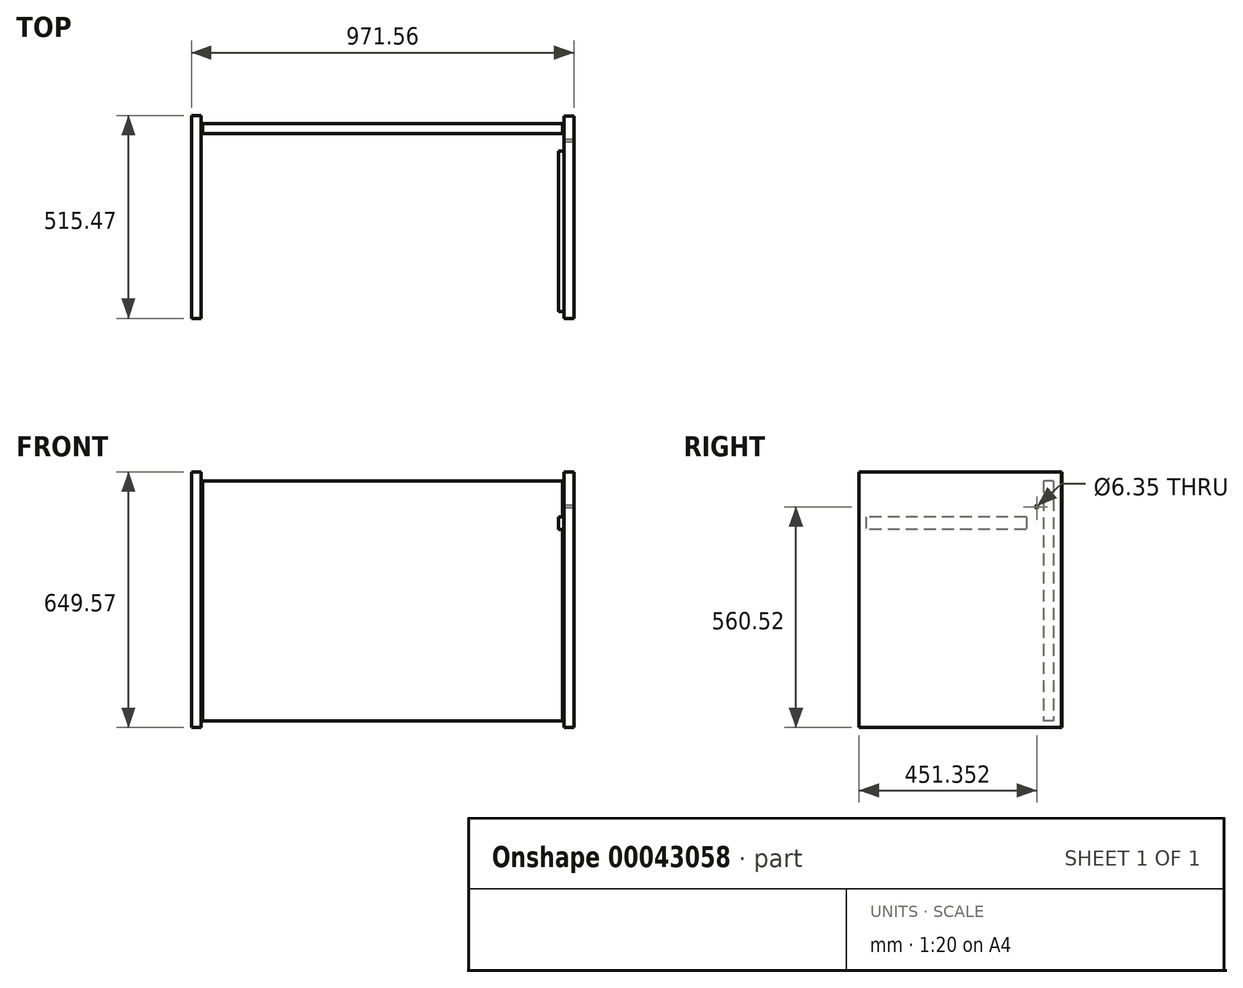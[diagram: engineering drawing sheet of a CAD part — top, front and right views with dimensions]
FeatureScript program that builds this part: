
annotation { "Feature Type Name" : "Feature", "Feature Type Description" : "" }
export const myFeature = defineFeature(function(context is Context, id is Id, definition is map)
    precondition{}
    {
        {
            var Q0;
            Q0=qCreatedBy(makeId("Front.planeOp"),FACE);
            var sketch = newSketch(context, id + "F0", { "sketchPlane" : qUnion([Q0])});
            skLineSegment(sketch, "E0.rect.bottom", {"start": v(457.2, 304.8) * mm, "end": v(-457.2, 304.8) * mm});
            skLineSegment(sketch, "E0.rect.top", {"start": v(457.2, -304.8) * mm, "end": v(-457.2, -304.8) * mm});
            skLineSegment(sketch, "E0.rect.left", {"start": v(457.2, 304.8) * mm, "end": v(457.2, -304.8) * mm});
            skLineSegment(sketch, "E0.rect.right", {"start": v(-457.2, 304.8) * mm, "end": v(-457.2, -304.8) * mm});
            skPoint(sketch, "E0.rect.middle", {"position": v(0, 0) * mm});
            skSolve(sketch);
        }
        {
            var Q0;
            Q0 = qSketchRegion(id + "F0", true);
            extrude(context, id + "F1", {"entities" : qUnion([Q0]), "oppositeDirection" : true, "depth" : 25.4 * mm});
        }
        {
            var Q0;
            Q0=makeQuery(id+"F1.opExtrude","SWEPT_FACE",FACE,{"disambiguationData":[OSD([sQuery(id+"F0.wireOp",EDGE,"E0.rect.left")])]});
            var sketch = newSketch(context, id + "F2", { "sketchPlane" : qUnion([Q0])});
            skLineSegment(sketch, "E1.bottom", {"start": v(45.61, 328.46) * mm, "end": v(-468.73, 328.46) * mm});
            skLineSegment(sketch, "E1.top", {"start": v(45.61, -320.5) * mm, "end": v(-468.73, -320.5) * mm});
            skLineSegment(sketch, "E1.left", {"start": v(45.61, 328.46) * mm, "end": v(45.61, -320.5) * mm});
            skLineSegment(sketch, "E1.right", {"start": v(-468.73, 328.46) * mm, "end": v(-468.73, -320.5) * mm});
            skSolve(sketch);
        }
        {
            var Q0;
            Q0 = qSketchRegion(id + "F2", true);
            extrude(context, id + "F3", {"entities" : qUnion([Q0]), "depth" : 28.57 * mm, "hasSecondDirection" : true, "secondDirectionOppositeDirection" : false, "secondDirectionDepth" : 3.17 * mm});
        }
        {
            var Q0;
            Q0=makeQuery(id+"F1.opExtrude","SWEPT_FACE",FACE,{"disambiguationData":[OSD([sQuery(id+"F0.wireOp",EDGE,"E0.rect.right")])]});
            var sketch = newSketch(context, id + "F4", { "sketchPlane" : qUnion([Q0])});
            skLineSegment(sketch, "E2.bottom", {"start": v(-46.65, 328.6) * mm, "end": v(468.82, 328.6) * mm});
            skLineSegment(sketch, "E2.top", {"start": v(-46.65, -320.96) * mm, "end": v(468.82, -320.96) * mm});
            skLineSegment(sketch, "E2.left", {"start": v(-46.65, 328.6) * mm, "end": v(-46.65, -320.96) * mm});
            skLineSegment(sketch, "E2.right", {"start": v(468.82, 328.6) * mm, "end": v(468.82, -320.96) * mm});
            skSolve(sketch);
        }
        {
            var Q0;
            Q0 = qSketchRegion(id + "F4", true);
            extrude(context, id + "F5", {"entities" : qUnion([Q0]), "depth" : 28.57 * mm, "hasSecondDirection" : true, "secondDirectionOppositeDirection" : false, "secondDirectionDepth" : 3.17 * mm});
        }
        {
            var Q0;
            Q0=makeQuery(id+"F3.opExtrude","CAP_FACE",FACE,{"disambiguationData":[OSD([sQuery(id+"F2.wireOp",EDGE,"E1.bottom"),sQuery(id+"F2.wireOp",EDGE,"E1.top"),sQuery(id+"F2.wireOp",EDGE,"E1.left"),sQuery(id+"F2.wireOp",EDGE,"E1.right")])],"isStart":true});
            var sketch = newSketch(context, id + "F6", { "sketchPlane" : qUnion([Q0])});
            skCircle(sketch, "E3", {"center": v(17.47, 239.56) * mm, "radius": 3.18 * mm});
            skSolve(sketch);
        }
        {
            var Q0;
            Q0 = qSketchRegion(id + "F6", true);
            extrude(context, id + "F7", {"entities" : qUnion([Q0]), "operationType" : NewBodyOperationType.REMOVE, "endBound" : BoundingType.THROUGH_ALL, "oppositeDirection" : true, "depth" : 25.4 * mm});
        }
        {
            var Q0;
            Q0=makeQuery(id+"F6.imprint","IMPRINT",FACE,{"disambiguationData":[TD([[makeQuery(id+"F6.imprint","IMPRINT",EDGE,{"derivedFrom":sQuery(id+"F6.wireOp",EDGE,"E3")}),-1.0]])]});
            var sketch = newSketch(context, id + "F8", { "sketchPlane" : qUnion([Q0])});
            skLineSegment(sketch, "E4.bottom", {"start": v(44.07, 214.16) * mm, "end": v(451.33, 214.16) * mm});
            skLineSegment(sketch, "E4.top", {"start": v(44.07, 182.39) * mm, "end": v(451.33, 182.39) * mm});
            skLineSegment(sketch, "E4.left", {"start": v(44.07, 214.16) * mm, "end": v(44.07, 182.39) * mm});
            skLineSegment(sketch, "E4.right", {"start": v(451.33, 214.16) * mm, "end": v(451.33, 182.39) * mm});
            skSolve(sketch);
        }
        {
            var Q0;
            Q0 = qSketchRegion(id + "F8", true);
            extrude(context, id + "F9", {"entities" : qUnion([Q0]), "depth" : 12.7 * mm});
        }
    });
